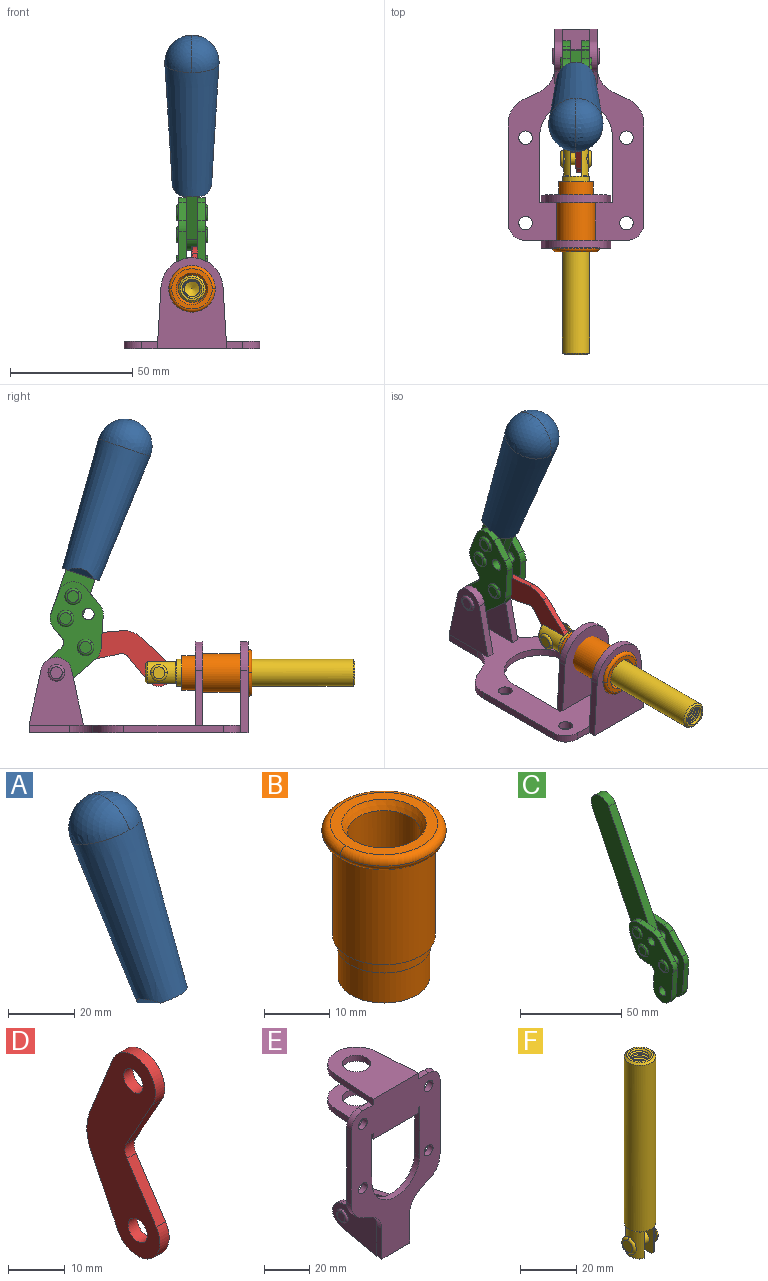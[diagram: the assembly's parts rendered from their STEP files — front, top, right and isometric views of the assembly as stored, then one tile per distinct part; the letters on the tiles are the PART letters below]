
ASSEMBLY  parts=6 mates=6
PART A: 11 faces, bbox 22.3x42.6x64.5 mm
  f0: sphere r=11.13mm, area 411.4mm2, adj f1,f8
  f1: cone r=11.11mm half-angle=3.3deg, axis (0,0.44,0.9), area 3251.8mm2, adj f0,f7,f8,f9,f10
  f2: cylinder r=6.16mm len=11.7mm, axis (1,0,0), area 89.5mm2, adj f3,f4,f5,f6
  f3: plane 60.23x36.75mm, normal (-1,0,0), area 763.6mm2, adj f2,f4,f6,f10
  f4: plane 51.37x25.05mm, normal (0,0.9,-0.44), area 264.2mm2, adj f2,f3,f5,f10
  f5: plane 60.23x36.75mm, normal (1,0,0), area 763.6mm2, adj f2,f4,f6,f10
  f6: plane 51.37x25.05mm, normal (0,-0.9,0.44), area 264.2mm2, adj f2,f3,f5,f10
  f7: plane 9.95x5.95mm, normal (0.71,-0.31,-0.64), area 25.8mm2, adj f1,f10
  f8: sphere r=11.13mm, area 411.4mm2, adj f0,f1
  f9: plane 9.95x5.95mm, normal (-0.71,-0.31,-0.64), area 25.8mm2, adj f1,f10
  f10: plane 14.27x11.38mm, normal (0,-0.44,-0.9), area 106.7mm2, adj f1,f3,f4,f5,f6,f7,f9
PART B: 15 faces, bbox 20.6x20.6x28.7 mm
  f0: torus R=8.26mm, axis (0,0,1), area 56.8mm2, adj f1,f10,f12
  f1: torus R=8.26mm, axis (0,0,1), area 56.8mm2, adj f0,f6,f13
  f2: cylinder r=5.59mm len=25.91mm, axis (0,0,1), area 909.6mm2, adj f3,f4
  f3: cone r=6.86mm half-angle=45deg, axis (0,0,-1), area 70.2mm2, adj f2,f14
  f4: cone r=6.47mm half-angle=30deg, axis (0,0,1), area 66.7mm2, adj f2,f13
  f5: cylinder r=7.04mm len=14.07mm, axis (0,0,1), area 252.6mm2, adj f11,f14
  f6: torus R=8.26mm, axis (0,0,1), area 56.8mm2, adj f1,f12,f13
  f7: cylinder r=7.16mm len=14.33mm, axis (0,0,1), area 91.5mm2, adj f9,f11
  f8: cylinder r=7.86mm len=18.42mm, axis (0,0,1), area 909.6mm2, adj f9,f10
  f9: plane 15.72x15.72mm, normal (0,0,-1), area 33mm2, adj f7,f8
  f10: plane 16.51x16.51mm, normal (0,0,-1), area 19.9mm2, adj f0,f8,f12
  f11: plane 14.33x14.33mm, normal (0,0,-1), area 5.7mm2, adj f5,f7
  f12: torus R=8.26mm, axis (0,0,1), area 56.8mm2, adj f0,f6,f10
  f13: plane 16.51x16.51mm, normal (0,0,1), area 82.7mm2, adj f1,f4,f6
  f14: plane 14.07x14.07mm, normal (0,0,-1), area 7.8mm2, adj f3,f5
PART C: 59 faces, bbox 12.9x60.2x99.6 mm
  f0: torus R=2.39mm, axis (-1,0,0), area 14.9mm2, adj f20,f43,f51
  f1: torus R=2.39mm, axis (-1,0,0), area 14.9mm2, adj f19,f42,f51
  f2: torus R=2.39mm, axis (-1,0,0), area 14.9mm2, adj f18,f35,f51
  f3: torus R=2.39mm, axis (-1,0,0), area 14.9mm2, adj f14,f17,f23
  f4: torus R=2.39mm, axis (-1,0,0), area 14.9mm2, adj f13,f16,f23
  f5: torus R=2.39mm, axis (-1,0,0), area 14.9mm2, adj f12,f15,f23
  f6: cylinder r=2.39mm len=4.78mm, axis (1,0,0), area 46.5mm2, adj f48,f50,f51
  f7: cylinder r=2.39mm len=4.78mm, axis (1,0,0), area 46.5mm2, adj f50,f51
  f8: cylinder r=6.35mm len=12.68mm, axis (1,0,0), area 61.8mm2, adj f38,f39,f50,f51
  f9: cylinder r=2.39mm len=4.78mm, axis (-1,0,0), area 70.5mm2, adj f46,f50
  f10: cylinder r=2.39mm len=4.78mm, axis (-1,0,0), area 46.5mm2, adj f23,f45,f46
  f11: cylinder r=2.39mm len=4.78mm, axis (-1,0,0), area 46.5mm2, adj f23,f46
  f12: plane 4.78x4.78mm, normal (1,0,0), area 17.9mm2, adj f5,f15
  f13: plane 4.78x4.78mm, normal (1,0,0), area 17.9mm2, adj f4,f16
  f14: plane 4.78x4.78mm, normal (1,0,0), area 17.9mm2, adj f3,f17
  f15: torus R=2.39mm, axis (-1,0,0), area 14.9mm2, adj f5,f12,f23
  f16: torus R=2.39mm, axis (-1,0,0), area 14.9mm2, adj f4,f13,f23
  f17: torus R=2.39mm, axis (-1,0,0), area 14.9mm2, adj f3,f14,f23
  f18: plane 4.78x4.78mm, normal (-1,0,0), area 17.9mm2, adj f2,f35
  f19: plane 4.78x4.78mm, normal (-1,0,0), area 17.9mm2, adj f1,f42
  f20: plane 4.78x4.78mm, normal (-1,0,0), area 17.9mm2, adj f0,f43
  f21: plane 2.26x0.2mm, normal (1,0,0), area 0.2mm2, adj f31,f44
  f22: plane 2.26x0.2mm, normal (-1,0,0), area 0.2mm2, adj f41,f44
  f23: plane 39.37x30.77mm, normal (1,0,0), area 565.5mm2, adj f3,f4,f5,f10,f11,f15,f16,f17
  f24: cylinder r=6.1mm len=4.15mm, axis (-1,0,0), area 14.7mm2, adj f23,f25,f32,f46
  f25: plane 10.25x9.01mm, normal (0,-0.75,0.66), area 42.3mm2, adj f23,f24,f26,f46
  f26: cylinder r=6.35mm len=4.64mm, axis (-1,0,0), area 15.6mm2, adj f23,f25,f27,f46
  f27: plane 15.84x3.1mm, normal (0,-1,-0.07), area 49.2mm2, adj f23,f26,f28,f46
  f28: cylinder r=6.35mm len=12.68mm, axis (-1,0,0), area 61.8mm2, adj f23,f27,f29,f46
  f29: plane 8.11x3.1mm, normal (0,1,0.07), area 25.2mm2, adj f23,f28,f30,f46
  f30: cylinder r=3.05mm len=3.25mm, axis (-1,0,0), area 14.8mm2, adj f23,f29,f31,f46
  f31: plane 5.99x3.1mm, normal (0,0.07,-1), area 18.6mm2, adj f21,f23,f30,f44,f46
  f32: plane 9.5x3.1mm, normal (0,-0.07,1), area 29.5mm2, adj f23,f24,f33,f46,f47
  f33: cylinder r=6.1mm len=8.63mm, axis (-1,0,0), area 39.1mm2, adj f23,f32,f34,f47
  f34: plane 8.65x3.96mm, normal (0,0.91,-0.42), area 29.5mm2, adj f23,f33,f44,f47
  f35: torus R=2.39mm, axis (-1,0,0), area 14.9mm2, adj f2,f18,f51
  f36: plane 10.25x9.01mm, normal (0,-0.75,0.66), area 42.3mm2, adj f37,f49,f50,f51
  f37: cylinder r=6.35mm len=4.64mm, axis (1,0,0), area 15.6mm2, adj f36,f38,f50,f51
  f38: plane 15.84x3.1mm, normal (0,-1,-0.07), area 49.2mm2, adj f8,f37,f50,f51
  f39: plane 8.11x3.1mm, normal (0,1,0.07), area 25.2mm2, adj f8,f40,f50,f51
  f40: cylinder r=3.05mm len=3.25mm, axis (1,0,0), area 14.8mm2, adj f39,f41,f50,f51
  f41: plane 5.99x3.1mm, normal (0,0.07,-1), area 18.6mm2, adj f22,f40,f44,f50,f51
  f42: torus R=2.39mm, axis (-1,0,0), area 14.9mm2, adj f1,f19,f51
  f43: torus R=2.39mm, axis (-1,0,0), area 14.9mm2, adj f0,f20,f51
  f44: cylinder r=6.35mm len=12.12mm, axis (-1,0,0), area 128.9mm2, adj f21,f22,f23,f31,f34,f41,f46,f47
  f45: plane 2.65x1.35mm, normal (1,0,0), area 1mm2, adj f10,f55
  f46: plane 39.08x20.42mm, normal (-1,0,0), area 412.5mm2, adj f9,f10,f11,f24,f25,f26,f27,f28
  f47: plane 77.62x39.82mm, normal (1,0,0), area 850mm2, adj f32,f33,f34,f44,f53,f54,f55
  f48: plane 2.65x1.35mm, normal (-1,0,0), area 1mm2, adj f6,f55
  f49: cylinder r=6.1mm len=4.15mm, axis (1,0,0), area 14.7mm2, adj f36,f50,f51,f56
  f50: plane 39.08x20.42mm, normal (1,0,0), area 412.5mm2, adj f6,f7,f8,f9,f36,f37,f38,f39
  f51: plane 39.37x30.77mm, normal (-1,0,0), area 565.5mm2, adj f0,f1,f2,f6,f7,f8,f35,f36
  f52: plane 8.65x3.96mm, normal (0,0.91,-0.42), area 29.5mm2, adj f44,f51,f57,f58
  f53: plane 68.49x33.4mm, normal (0,0.9,-0.44), area 358.1mm2, adj f44,f47,f54,f58
  f54: cylinder r=6.35mm len=12.06mm, axis (1,0,0), area 93.7mm2, adj f47,f53,f55,f58
  f55: plane 68.49x33.4mm, normal (0,-0.9,0.44), area 358.1mm2, adj f44,f45,f46,f47,f48,f50,f54,f58
  f56: plane 9.5x3.1mm, normal (0,-0.07,1), area 29.5mm2, adj f49,f50,f51,f57,f58
  f57: cylinder r=6.1mm len=8.63mm, axis (1,0,0), area 39.1mm2, adj f51,f52,f56,f58
  f58: plane 77.62x39.82mm, normal (-1,0,0), area 850mm2, adj f44,f52,f53,f54,f55,f56,f57
PART D: 12 faces, bbox 2.3x18.2x42.8 mm
  f0: cylinder r=2.4mm len=4.8mm, axis (1,0,0), area 34.9mm2, adj f4,f11
  f1: cylinder r=10.41mm len=8.47mm, axis (1,0,0), area 20.2mm2, adj f4,f9,f10,f11
  f2: cylinder r=3.05mm len=3.16mm, axis (1,0,0), area 7.7mm2, adj f4,f6,f7,f11
  f3: cylinder r=2.4mm len=4.8mm, axis (1,0,0), area 34.9mm2, adj f4,f11
  f4: plane 42.81x18.23mm, normal (-1,0,0), area 414.1mm2, adj f0,f1,f2,f3,f5,f6,f7,f8
  f5: cylinder r=5.54mm len=10.67mm, axis (1,0,0), area 41.8mm2, adj f4,f6,f10,f11
  f6: plane 11.66x6.53mm, normal (0,-0.87,-0.49), area 30.9mm2, adj f2,f4,f5,f11
  f7: plane 11.17x7.33mm, normal (0,-0.84,0.55), area 30.9mm2, adj f2,f4,f8,f11
  f8: cylinder r=5.54mm len=10.51mm, axis (1,0,0), area 41.8mm2, adj f4,f7,f9,f11
  f9: plane 13.67x6.67mm, normal (0,0.9,-0.44), area 35.1mm2, adj f1,f4,f8,f11
  f10: plane 14.1x5.7mm, normal (0,0.93,0.37), area 35.1mm2, adj f1,f4,f5,f11
  f11: plane 42.81x18.23mm, normal (1,0,0), area 414.1mm2, adj f0,f1,f2,f3,f5,f6,f7,f8
PART E: 55 faces, bbox 55.7x37.4x89.8 mm
  f0: torus R=2.41mm, axis (-1,0,0), area 15mm2, adj f11,f15,f25
  f1: torus R=2.41mm, axis (-1,0,0), area 15mm2, adj f10,f12,f22
  f2: cylinder r=2.78mm len=5.56mm, axis (0,-1,0), area 54.2mm2, adj f30,f54
  f3: cylinder r=14.99mm len=29.97mm, axis (0,-1,0), area 145.9mm2, adj f30,f49,f53,f54
  f4: cylinder r=2.78mm len=5.56mm, axis (0,-1,0), area 54.2mm2, adj f30,f54
  f5: cylinder r=2.78mm len=5.56mm, axis (0,-1,0), area 54.2mm2, adj f30,f54
  f6: cylinder r=2.78mm len=5.56mm, axis (0,-1,0), area 54.2mm2, adj f30,f54
  f7: cylinder r=6.35mm len=12.7mm, axis (0,0,1), area 123.6mm2, adj f27,f51
  f8: cylinder r=6.35mm len=12.7mm, axis (0,0,-1), area 124.7mm2, adj f21,f35
  f9: cylinder r=2.41mm len=11.18mm, axis (-1,0,0), area 169.4mm2, adj f16,f19
  f10: plane 4.83x4.83mm, normal (1,0,0), area 18.3mm2, adj f1,f12
  f11: plane 4.83x4.83mm, normal (-1,0,0), area 18.3mm2, adj f0,f15
  f12: torus R=2.41mm, axis (-1,0,0), area 15mm2, adj f1,f10,f22
  f13: cylinder r=6.35mm len=12.41mm, axis (1,0,0), area 53.4mm2, adj f18,f19,f22,f23
  f14: cylinder r=6.35mm len=12.41mm, axis (-1,0,0), area 53.4mm2, adj f16,f17,f24,f25
  f15: torus R=2.41mm, axis (-1,0,0), area 15mm2, adj f0,f11,f25
  f16: plane 27.86x22.35mm, normal (1,0,0), area 425.4mm2, adj f9,f14,f17,f24,f30
  f17: plane 22.86x4.97mm, normal (0,0.21,0.98), area 72.5mm2, adj f14,f16,f25,f30
  f18: plane 22.86x4.97mm, normal (0,0.21,0.98), area 72.5mm2, adj f13,f19,f22,f30
  f19: plane 27.86x22.35mm, normal (-1,0,0), area 425.4mm2, adj f9,f13,f18,f23,f30
  f20: cylinder r=12.7mm len=25.35mm, axis (0,0,-1), area 119.8mm2, adj f21,f34,f35,f36
  f21: plane 34.21x28.07mm, normal (0,0,-1), area 702.4mm2, adj f8,f20,f30,f34,f36
  f22: plane 27.96x22.45mm, normal (1,0,0), area 407.2mm2, adj f1,f12,f13,f18,f23,f30,f42,f43
  f23: plane 22.86x4.97mm, normal (0,0.21,-0.98), area 72.5mm2, adj f13,f19,f22,f44
  f24: plane 22.86x4.97mm, normal (0,0.21,-0.98), area 72.5mm2, adj f14,f16,f25,f44
  f25: plane 27.86x22.35mm, normal (-1,0,0), area 407.1mm2, adj f0,f14,f15,f17,f24,f30,f45,f46
  f26: plane 3.1x0.95mm, normal (0,0,-1), area 2.7mm2, adj f30,f49,f50,f54
  f27: plane 34.21x28.07mm, normal (0,0,1), area 702.4mm2, adj f7,f28,f30,f50,f52
  f28: cylinder r=12.7mm len=25.35mm, axis (0,0,1), area 118.8mm2, adj f27,f50,f51,f52
  f29: plane 3.1x0.95mm, normal (0,0,-1), area 2.7mm2, adj f30,f52,f53,f54
  f30: plane 86.54x55.63mm, normal (0,1,0), area 2362.9mm2, adj f2,f3,f4,f5,f6,f16,f17,f18
  f31: plane 40.56x3.1mm, normal (-1,0,0), area 125.7mm2, adj f30,f32,f48,f54
  f32: cylinder r=7.11mm len=7.11mm, axis (0,-1,0), area 34.6mm2, adj f30,f31,f33,f54
  f33: plane 6.67x3.1mm, normal (0,0,1), area 20.4mm2, adj f30,f32,f34,f54
  f34: plane 25.39x3.13mm, normal (-1,0.06,0), area 79.5mm2, adj f20,f21,f33,f35,f54
  f35: plane 37.31x28.45mm, normal (0,0,1), area 789.9mm2, adj f8,f20,f34,f36,f54
  f36: plane 25.39x3.13mm, normal (1,0.06,0), area 79.5mm2, adj f20,f21,f35,f37,f54
  f37: plane 6.67x3.1mm, normal (0,0,1), area 20.4mm2, adj f30,f36,f38,f54
  f38: cylinder r=7.11mm len=7.11mm, axis (0,-1,0), area 34.6mm2, adj f30,f37,f39,f54
  f39: plane 40.56x3.1mm, normal (1,0,0), area 125.7mm2, adj f30,f38,f40,f54
  f40: cylinder r=11.18mm len=10.16mm, axis (0,-1,0), area 39.5mm2, adj f30,f39,f41,f54
  f41: plane 6.09x3.1mm, normal (0.42,0,-0.91), area 20.8mm2, adj f30,f40,f42,f54
  f42: cylinder r=11.18mm len=9.41mm, axis (0,-1,0), area 37.2mm2, adj f22,f30,f41,f43,f54
  f43: plane 16.5x3.1mm, normal (1,0,0), area 51.1mm2, adj f22,f42,f44,f54
  f44: plane 17.37x3.1mm, normal (0,0,-1), area 53.8mm2, adj f23,f24,f30,f43,f45,f54
  f45: plane 16.5x3.1mm, normal (-1,0,0), area 51.1mm2, adj f25,f44,f46,f54
  f46: cylinder r=11.18mm len=9.41mm, axis (0,-1,0), area 37.2mm2, adj f25,f30,f45,f47,f54
  f47: plane 6.09x3.1mm, normal (-0.42,0,-0.91), area 20.8mm2, adj f30,f46,f48,f54
  f48: cylinder r=11.18mm len=10.16mm, axis (0,-1,0), area 39.5mm2, adj f30,f31,f47,f54
  f49: plane 26.54x3.1mm, normal (-1,0,0), area 82.3mm2, adj f3,f26,f30,f54
  f50: plane 25.39x3.1mm, normal (1,0.06,0), area 78.8mm2, adj f26,f27,f28,f51,f54
  f51: plane 37.31x28.45mm, normal (0,0,-1), area 789.9mm2, adj f7,f28,f50,f52,f54
  f52: plane 25.39x3.1mm, normal (-1,0.06,0), area 78.8mm2, adj f27,f28,f29,f51,f54
  f53: plane 26.54x3.1mm, normal (1,0,0), area 82.3mm2, adj f3,f29,f30,f54
  f54: plane 89.66x55.63mm, normal (0,-1,0), area 2678.5mm2, adj f2,f3,f4,f5,f6,f26,f29,f31
PART F: 48 faces, bbox 12.6x11.1x86.1 mm
  f0: torus R=2.41mm, axis (-1,0,0), area 15mm2, adj f30,f32,f34
  f1: torus R=2.41mm, axis (-1,0,0), area 15mm2, adj f29,f31,f33
  f2: cylinder r=5.54mm len=72.39mm, axis (0,0,1), area 2518.5mm2, adj f3,f4,f42,f43
  f3: cone r=5.54mm half-angle=45deg, axis (0,0,1), area 7.6mm2, adj f2,f5,f41
  f4: cone r=5.54mm half-angle=45deg, axis (0,0,-1), area 34.9mm2, adj f2,f39
  f5: cylinder r=5.08mm len=11.48mm, axis (0,0,1), area 108.3mm2, adj f3,f7,f8,f41
  f6: cylinder r=2.41mm len=4.83mm, axis (-1,0,0), area 71.2mm2, adj f40,f41
  f7: cylinder r=2.41mm len=4.83mm, axis (-1,0,0), area 7.6mm2, adj f5,f34
  f8: cone r=5.08mm half-angle=45deg, axis (0,0,1), area 10.6mm2, adj f5,f37,f41
  f9: cone r=3.98mm half-angle=45deg, axis (0,0,1), area 17.6mm2, adj f27,f39,f45,f46,f47
  f10: cylinder r=2.41mm len=4.83mm, axis (-1,0,0), area 7.6mm2, adj f33,f38
  f11: cylinder r=3.2mm len=6.4mm, axis (0,0,1), area 78.4mm2, adj f12,f28,f44,f45,f47
  f12: cylinder r=3.2mm len=6.4mm, axis (0,0,1), area 10.5mm2, adj f11,f13,f45,f47
  f13: cylinder r=3.2mm len=6.4mm, axis (0,0,1), area 10.5mm2, adj f12,f14,f45,f47
  f14: cylinder r=3.2mm len=6.4mm, axis (0,0,1), area 10.5mm2, adj f13,f15,f45,f47
  f15: cylinder r=3.2mm len=6.4mm, axis (0,0,1), area 10.5mm2, adj f14,f16,f45,f47
  f16: cylinder r=3.2mm len=6.4mm, axis (0,0,1), area 10.5mm2, adj f15,f17,f45,f47
  f17: cylinder r=3.2mm len=6.4mm, axis (0,0,1), area 10.5mm2, adj f16,f18,f45,f47
  f18: cylinder r=3.2mm len=6.4mm, axis (0,0,1), area 10.5mm2, adj f17,f19,f45,f47
  f19: cylinder r=3.2mm len=6.4mm, axis (0,0,1), area 10.5mm2, adj f18,f20,f45,f47
  f20: cylinder r=3.2mm len=6.4mm, axis (0,0,1), area 10.5mm2, adj f19,f21,f45,f47
  f21: cylinder r=3.2mm len=6.4mm, axis (0,0,1), area 10.5mm2, adj f20,f22,f45,f47
  f22: cylinder r=3.2mm len=6.4mm, axis (0,0,1), area 10.5mm2, adj f21,f23,f45,f47
  f23: cylinder r=3.2mm len=6.4mm, axis (0,0,1), area 10.5mm2, adj f22,f24,f45,f47
  f24: cylinder r=3.2mm len=6.4mm, axis (0,0,1), area 10.5mm2, adj f23,f25,f45,f47
  f25: cylinder r=3.2mm len=6.4mm, axis (0,0,1), area 10.5mm2, adj f24,f26,f45,f47
  f26: cylinder r=3.2mm len=6.4mm, axis (0,0,1), area 10.5mm2, adj f25,f27,f45,f47
  f27: cylinder r=3.2mm len=6.4mm, axis (0,0,1), area 7.4mm2, adj f9,f26,f45,f47
  f28: cone r=3.2mm half-angle=60deg, axis (0,0,1), area 37.2mm2, adj f11
  f29: plane 4.83x4.83mm, normal (-1,0,0), area 18.3mm2, adj f1,f31
  f30: plane 4.83x4.83mm, normal (1,0,0), area 18.3mm2, adj f0,f32
  f31: torus R=2.41mm, axis (-1,0,0), area 15mm2, adj f1,f29,f33
  f32: torus R=2.41mm, axis (-1,0,0), area 15mm2, adj f0,f30,f34
  f33: plane 6.83x6.83mm, normal (1,0,0), area 18.3mm2, adj f1,f10,f31
  f34: plane 6.83x6.83mm, normal (-1,0,0), area 18.3mm2, adj f0,f7,f32
  f35: cone r=5.08mm half-angle=45deg, axis (0,0,1), area 10.6mm2, adj f36,f38,f40
  f36: plane 7.25x1.97mm, normal (0,0,-1), area 10mm2, adj f35,f40
  f37: plane 7.25x1.97mm, normal (0,0,-1), area 10mm2, adj f8,f41
  f38: cylinder r=5.08mm len=11.48mm, axis (0,0,1), area 108.3mm2, adj f10,f35,f40,f42
  f39: plane 9.55x9.55mm, normal (0,0,1), area 22mm2, adj f4,f9
  f40: plane 12.76x10.09mm, normal (1,0,0), area 95.7mm2, adj f6,f35,f36,f38,f42,f43
  f41: plane 12.76x10.09mm, normal (-1,0,0), area 95.7mm2, adj f3,f5,f6,f8,f37,f43
  f42: cone r=5.54mm half-angle=45deg, axis (0,0,1), area 7.6mm2, adj f2,f38,f40
  f43: plane 11.07x4.7mm, normal (0,0,-1), area 50.4mm2, adj f2,f40,f41
  f44: plane 0.89x0.62mm, normal (-1,0,0), area 0.3mm2, adj f11,f45,f46,f47
  f45: bspline ~24.8x7.63mm, area 266.6mm2, adj f9,f11,f12,f13,f14,f15,f16,f17
  f46: bspline ~24.87x7.63mm, area 73.6mm2, adj f9,f44,f45,f47
  f47: bspline ~24.98x7.63mm, area 272.5mm2, adj f9,f11,f12,f13,f14,f15,f16,f17
PLACE A rot(axis=(1,0,0),45deg) t=(-0.04,-6.77,29.9)mm
PLACE B rot(axis=(1,0,0),90deg) t=(0,2.25,0)mm
PLACE C rot(axis=(1,0,0),45deg) t=(0,-6.77,29.9)mm
PLACE D rot(axis=(1,0,0),111.1deg) t=(1.16,14.66,7.24)mm
PLACE E rot(axis=(1,0,0),90deg) t=(0,1.23,0)mm fixed
PLACE F rot(axis=(1,0,0),90deg) t=(0,6.82,0)mm
MATE slider F.f2 <-> E.f7  axis (0,-1,0) through (0,-51.96,24.61)mm
MATE fastened B.f2 <-> E.f7  axis (0,-1,0) through (0,-45.16,24.61)mm
MATE revolute D.f3 <-> C.f4  axis (1,0,0) through (0,21.34,35.03)mm
MATE revolute D.f0 <-> F.f6  axis (-1,0,0) through (0,-8.65,24.61)mm
MATE fastened C.f54 <-> A.f2  axis (-1,0,0) through (-2.35,4.73,118.87)mm
MATE revolute C.f7 <-> E.f0  axis (1,0,0) through (0,33.32,24.61)mm
